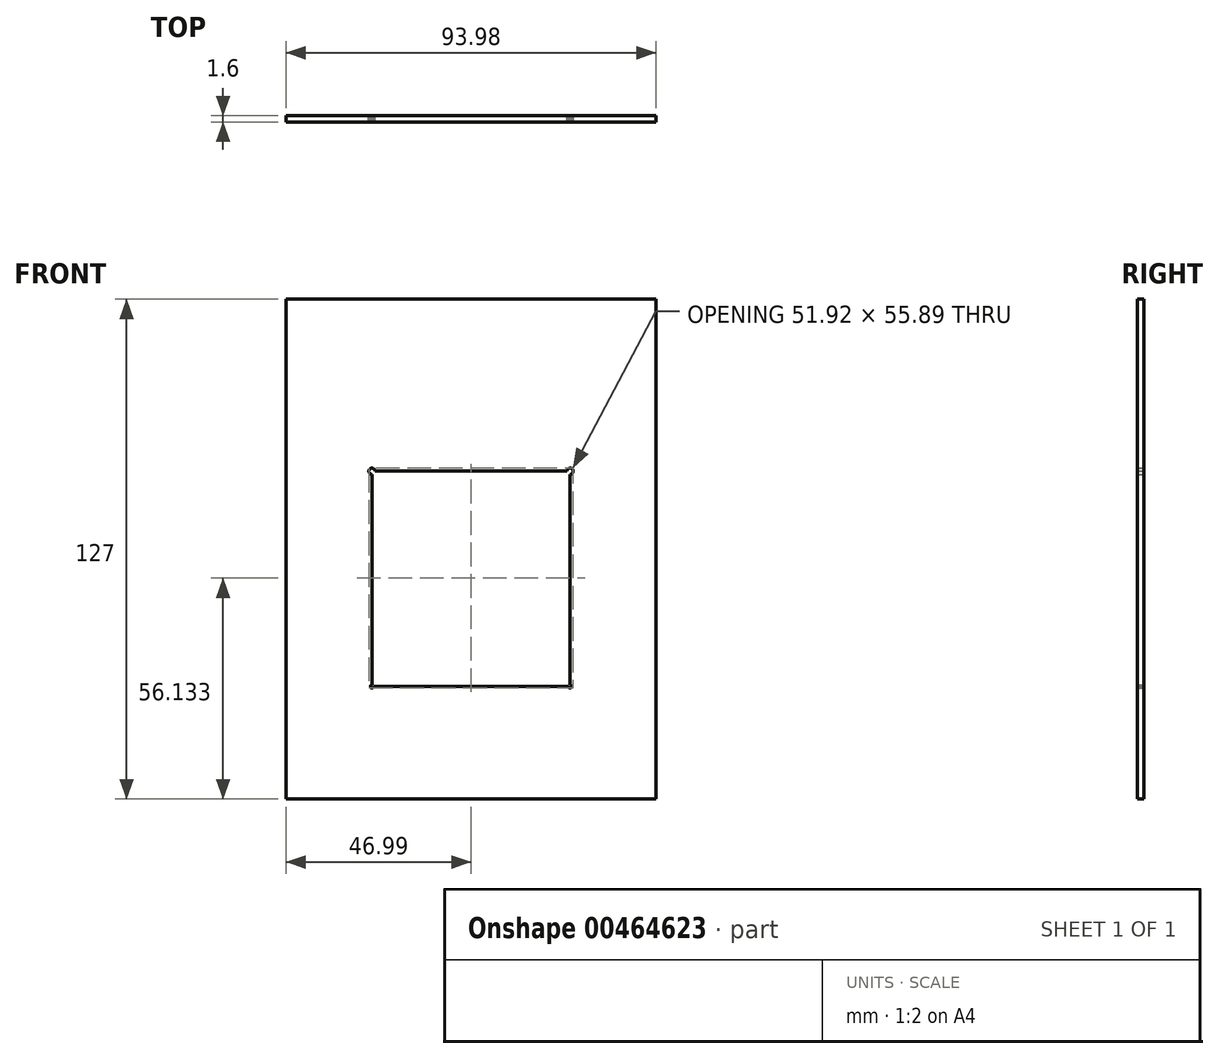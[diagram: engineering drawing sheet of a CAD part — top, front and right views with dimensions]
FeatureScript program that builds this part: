
annotation { "Feature Type Name" : "Feature", "Feature Type Description" : "" }
export const myFeature = defineFeature(function(context is Context, id is Id, definition is map)
    precondition{}
    {
        {
            var Q0;
            Q0=qCreatedBy(makeId("Front.planeOp"),FACE);
            var sketch = newSketch(context, id + "F0", { "sketchPlane" : qUnion([Q0])});
            skLineSegment(sketch, "E0.bottom", {"start": v(-47, 71.06) * mm, "end": v(46.99, 71.06) * mm});
            skLineSegment(sketch, "E0.top", {"start": v(-47, -55.94) * mm, "end": v(46.99, -55.94) * mm});
            skLineSegment(sketch, "E0.left", {"start": v(-47, 71.06) * mm, "end": v(-47, -55.94) * mm});
            skLineSegment(sketch, "E0.right", {"start": v(47, 71.06) * mm, "end": v(46.99, -55.94) * mm});
            skLineSegment(sketch, "E1.bottom", {"start": v(-25.19, 27.36) * mm, "end": v(25.19, 27.36) * mm});
            skLineSegment(sketch, "E1.top", {"start": v(-25.19, -27.36) * mm, "end": v(25.19, -27.36) * mm});
            skLineSegment(sketch, "E1.left", {"start": v(-25.19, 27.36) * mm, "end": v(-25.19, -27.36) * mm});
            skLineSegment(sketch, "E1.right", {"start": v(25.19, 27.36) * mm, "end": v(25.19, -27.36) * mm});
            skLineSegment(sketch, "E2", {"start": v(25.19, 27.36) * mm, "end": v(-25.19, -27.36) * mm, "construction": true});
            skArc(sketch, "E3", {"start": v(-24.4, 27.36) * mm, "mid": v(-25.75, 27.92) * mm, "end": v(-25.19, 26.58) * mm});
            skArc(sketch, "E4", {"start": v(25.19, 26.58) * mm, "mid": v(25.75, 27.92) * mm, "end": v(24.4, 27.36) * mm});
            skArc(sketch, "E5", {"start": v(-25.19, -26.97) * mm, "mid": v(-25.47, -27.64) * mm, "end": v(-24.8, -27.36) * mm});
            skArc(sketch, "E6", {"start": v(24.8, -27.36) * mm, "mid": v(25.47, -27.64) * mm, "end": v(25.19, -26.97) * mm});
            skSolve(sketch);
        }
        {
            var Q0;
            Q0=makeQuery(id+"F0.imprint","IMPRINT",FACE,{"disambiguationData":[TD([[makeQuery(id+"F0.imprint","IMPRINT",EDGE,{"derivedFrom":sQuery(id+"F0.wireOp",EDGE,"E0.bottom")}),-1.0]])]});
            var Q1;
            Q1=sQuery(id+"F0.wireOp",EDGE,"E1.bottom");
            var Q2;
            Q2=sQuery(id+"F0.wireOp",EDGE,"E1.left");
            var Q3;
            Q3=sQuery(id+"F0.wireOp",EDGE,"E1.right");
            var Q4;
            Q4=sQuery(id+"F0.wireOp",EDGE,"E1.top");
            var Q5;
            Q5=sQuery(id+"F0.wireOp",EDGE,"E0.bottom");
            extrude(context, id + "F1", {"entities" : qUnion([Q0]), "surfaceEntities" : qUnion([Q1, Q2, Q3, Q4, Q5]), "offsetDistance" : 25.4 * mm, "depth" : 1.6 * mm});
        }
    });
